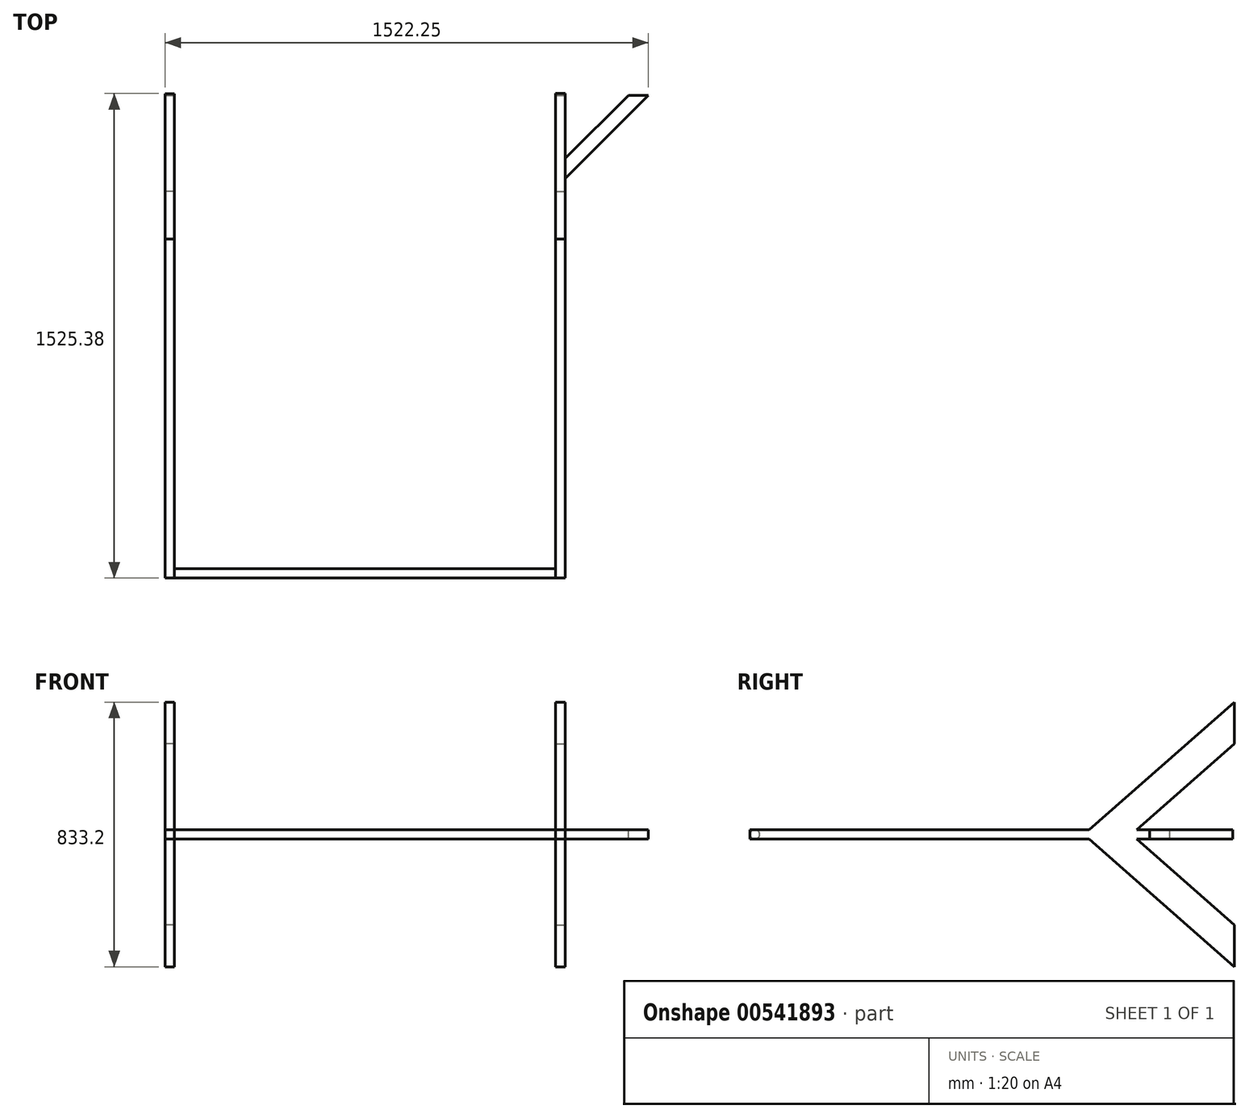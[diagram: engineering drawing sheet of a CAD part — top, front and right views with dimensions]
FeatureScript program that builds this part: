
annotation { "Feature Type Name" : "Feature", "Feature Type Description" : "" }
export const myFeature = defineFeature(function(context is Context, id is Id, definition is map)
    precondition{}
    {
        {
            var Q0;
            Q0=qCreatedBy(makeId("Front.planeOp"),FACE);
            var sketch = newSketch(context, id + "F0", { "sketchPlane" : qUnion([Q0])});
            skLineSegment(sketch, "E0.bottom", {"start": v(-147.04, 19) * mm, "end": v(-117.04, 19) * mm});
            skLineSegment(sketch, "E0.top", {"start": v(-147.04, -11) * mm, "end": v(-117.04, -11) * mm});
            skLineSegment(sketch, "E0.left", {"start": v(-147.04, 19) * mm, "end": v(-147.04, -11) * mm});
            skLineSegment(sketch, "E0.right", {"start": v(-117.04, 19) * mm, "end": v(-117.04, -11) * mm});
            skLineSegment(sketch, "E1.bottom", {"start": v(1082.96, 19) * mm, "end": v(1112.95, 19) * mm});
            skLineSegment(sketch, "E1.top", {"start": v(1082.96, -11) * mm, "end": v(1112.95, -11) * mm});
            skLineSegment(sketch, "E1.left", {"start": v(1082.96, 19) * mm, "end": v(1082.96, -11) * mm});
            skLineSegment(sketch, "E1.right", {"start": v(1112.95, 19) * mm, "end": v(1112.95, -11) * mm});
            skSolve(sketch);
        }
        {
            var Q0;
            Q0 = qSketchRegion(id + "F0", true);
            extrude(context, id + "F1", {"entities" : qUnion([Q0]), "depth" : 1520 * mm, "offsetDistance" : 25.4 * mm});
        }
        {
            var Q0;
            Q0=makeQuery(id+"F1.opExtrude","SWEPT_FACE",FACE,{"disambiguationData":[OSD([sQuery(id+"F0.wireOp",EDGE,"E0.right")])]});
            var sketch = newSketch(context, id + "F2", { "sketchPlane" : qUnion([Q0])});
            skCircle(sketch, "E2", {"center": v(-1505, 4) * mm, "radius": 15 * mm});
            skSolve(sketch);
        }
        {
            var Q0;
            Q0=makeQuery(id+"F2.imprint","IMPRINT",FACE,{"disambiguationData":[TD([[makeQuery(id+"F2.imprint","IMPRINT",EDGE,{"derivedFrom":sQuery(id+"F2.wireOp",EDGE,"E2")}),1.0]])]});
            extrude(context, id + "F3", {"entities" : qUnion([Q0]), "depth" : 1200 * mm, "offsetDistance" : 25.4 * mm});
        }
        {
            var Q0;
            {var subQ2=sQuery(id+"FY8PT7J0VQWQwk3_3.wireOp",EDGE,"tGojgUX5-YvZo-xwas-wiyC-chnQ7OWjS32x");var subQ6=sQuery(id+"F0.wireOp",EDGE,"E1.bottom");Q0=makeQuery(id+"F4df56pYNSQ6nNV_3.boolean.opBoolean","SPLIT",FACE,{"disambiguationData":[TD([makeQuery(id+"F4df56pYNSQ6nNV_3.opExtrude","SWEPT_FACE",FACE,{"disambiguationData":[OSD([subQ2])]})])],"derivedFrom":makeQuery(id+"F1.opExtrude","SWEPT_FACE",FACE,{"disambiguationData":[OSD([subQ6])]})});}
            var sketch = newSketch(context, id + "F4", { "sketchPlane" : qUnion([Q0])});
            skLineSegment(sketch, "E3", {"start": v(1097.02, -71.2) * mm, "end": v(1097.02, -202.42) * mm, "construction": true});
            skLineSegment(sketch, "E4.MirrorCS", {"start": v(1375.21, 0) * mm, "end": v(1312.02, 0) * mm});
            skLineSegment(sketch, "E5.MirrorCS", {"start": v(1112.02, -200) * mm, "end": v(1312.02, 0) * mm});
            skLineSegment(sketch, "E6.MirrorCS", {"start": v(1112.02, -263.2) * mm, "end": v(1375.21, 0) * mm});
            skLineSegment(sketch, "E7.MirrorCS", {"start": v(1112.02, -200) * mm, "end": v(1112.02, -263.2) * mm});
            skSolve(sketch);
        }
        {
            var Q0;
            Q0=makeQuery(id+"F4.imprint","IMPRINT",FACE,{"disambiguationData":[TD([[makeQuery(id+"F4.imprint","IMPRINT",EDGE,{"derivedFrom":sQuery(id+"F4.wireOp",EDGE,"b17f032c-e895-4f8e-90fb-e392f7050fe5")}),1.0]])]});
            var Q1;
            Q1=makeQuery(id+"F4.imprint","IMPRINT",FACE,{"disambiguationData":[TD([[makeQuery(id+"F4.imprint","IMPRINT",EDGE,{"derivedFrom":sQuery(id+"F4.wireOp",EDGE,"E4.MirrorCS")}),1.0]])]});
            extrude(context, id + "F5", {"entities" : qUnion([Q0, Q1]), "operationType" : NewBodyOperationType.ADD, "oppositeDirection" : true, "depth" : 30 * mm, "offsetDistance" : 25.4 * mm});
        }
        {
            var Q0;
            Q0=makeQuery(id+"F1.opExtrude","SWEPT_FACE",FACE,{"disambiguationData":[OSD([sQuery(id+"F0.wireOp",EDGE,"E0.left")])]});
            var sketch = newSketch(context, id + "F6", { "sketchPlane" : qUnion([Q0])});
            skLineSegment(sketch, "E8", {"start": v(302.6, -11) * mm, "end": v(-5.17, -281) * mm});
            skLineSegment(sketch, "E9", {"start": v(452.6, -11) * mm, "end": v(-5.17, -412.6) * mm});
            skLineSegment(sketch, "E10", {"start": v(-5.17, -412.6) * mm, "end": v(-5.17, -281) * mm});
            skLineSegment(sketch, "E11", {"start": v(302.6, -11) * mm, "end": v(452.6, -11) * mm});
            skLineSegment(sketch, "E12.MirrorCS", {"start": v(302.6, 19) * mm, "end": v(452.6, 19) * mm});
            skLineSegment(sketch, "E13", {"start": v(0, 4) * mm, "end": v(64.02, 4) * mm, "construction": true});
            skLineSegment(sketch, "E14.MirrorCS", {"start": v(452.6, 19) * mm, "end": v(-5.17, 420.6) * mm});
            skLineSegment(sketch, "E15.MirrorCS", {"start": v(302.6, 19) * mm, "end": v(-5.17, 289) * mm});
            skLineSegment(sketch, "E16.MirrorCS", {"start": v(-5.17, 420.6) * mm, "end": v(-5.17, 289) * mm});
            skSolve(sketch);
        }
        {
            var Q0;
            Q0=makeQuery(id+"F6.imprint","IMPRINT",FACE,{"disambiguationData":[TD([[makeQuery(id+"F6.imprint","IMPRINT",EDGE,{"derivedFrom":sQuery(id+"F6.wireOp",EDGE,"E12.MirrorCS")}),-1.0]])]});
            var Q1;
            Q1=makeQuery(id+"F6.imprint","IMPRINT",FACE,{"disambiguationData":[TD([[makeQuery(id+"F6.imprint","IMPRINT",EDGE,{"derivedFrom":sQuery(id+"F6.wireOp",EDGE,"E8")}),1.0]])]});
            extrude(context, id + "F7", {"entities" : qUnion([Q0, Q1]), "operationType" : NewBodyOperationType.ADD, "oppositeDirection" : true, "depth" : 30 * mm, "offsetDistance" : 25.4 * mm});
        }
        {
            var Q0;
            {var subQ0=sQuery(id+"F4.wireOp",EDGE,"E6.MirrorCS");var subQ3=sQuery(id+"F0.wireOp",EDGE,"E1.right");Q0=makeQuery(id+"F5.boolean.opBoolean","SPLIT",FACE,{"disambiguationData":[TD([makeQuery(id+"F5.opExtrude","SWEPT_FACE",FACE,{"disambiguationData":[OSD([subQ0])]})])],"derivedFrom":makeQuery(id+"F1.opExtrude","SWEPT_FACE",FACE,{"disambiguationData":[OSD([subQ3])]})});}
            var sketch = newSketch(context, id + "F8", { "sketchPlane" : qUnion([Q0])});
            skLineSegment(sketch, "E17", {"start": v(-302.38, 19) * mm, "end": v(5.38, 289) * mm});
            skLineSegment(sketch, "E18", {"start": v(-452.38, 19) * mm, "end": v(5.38, 420.6) * mm});
            skLineSegment(sketch, "E19", {"start": v(5.38, 420.6) * mm, "end": v(5.38, 289) * mm});
            skLineSegment(sketch, "E20", {"start": v(-302.38, 19) * mm, "end": v(-452.38, 19) * mm});
            skLineSegment(sketch, "E21.MirrorCS", {"start": v(-302.38, -11) * mm, "end": v(-452.38, -11) * mm});
            skLineSegment(sketch, "E22", {"start": v(0.21, 4) * mm, "end": v(-63.8, 4) * mm, "construction": true});
            skLineSegment(sketch, "E23.MirrorCS", {"start": v(-452.38, -11) * mm, "end": v(5.38, -412.6) * mm});
            skLineSegment(sketch, "E24.MirrorCS", {"start": v(-302.38, -11) * mm, "end": v(5.38, -281) * mm});
            skLineSegment(sketch, "E25.MirrorCS", {"start": v(5.38, -412.6) * mm, "end": v(5.38, -281) * mm});
            skSolve(sketch);
        }
        {
            var Q0;
            Q0 = qSketchRegion(id + "F8", true);
            extrude(context, id + "F9", {"entities" : qUnion([Q0]), "operationType" : NewBodyOperationType.ADD, "oppositeDirection" : true, "depth" : 30 * mm, "offsetDistance" : 25.4 * mm});
        }
    });
